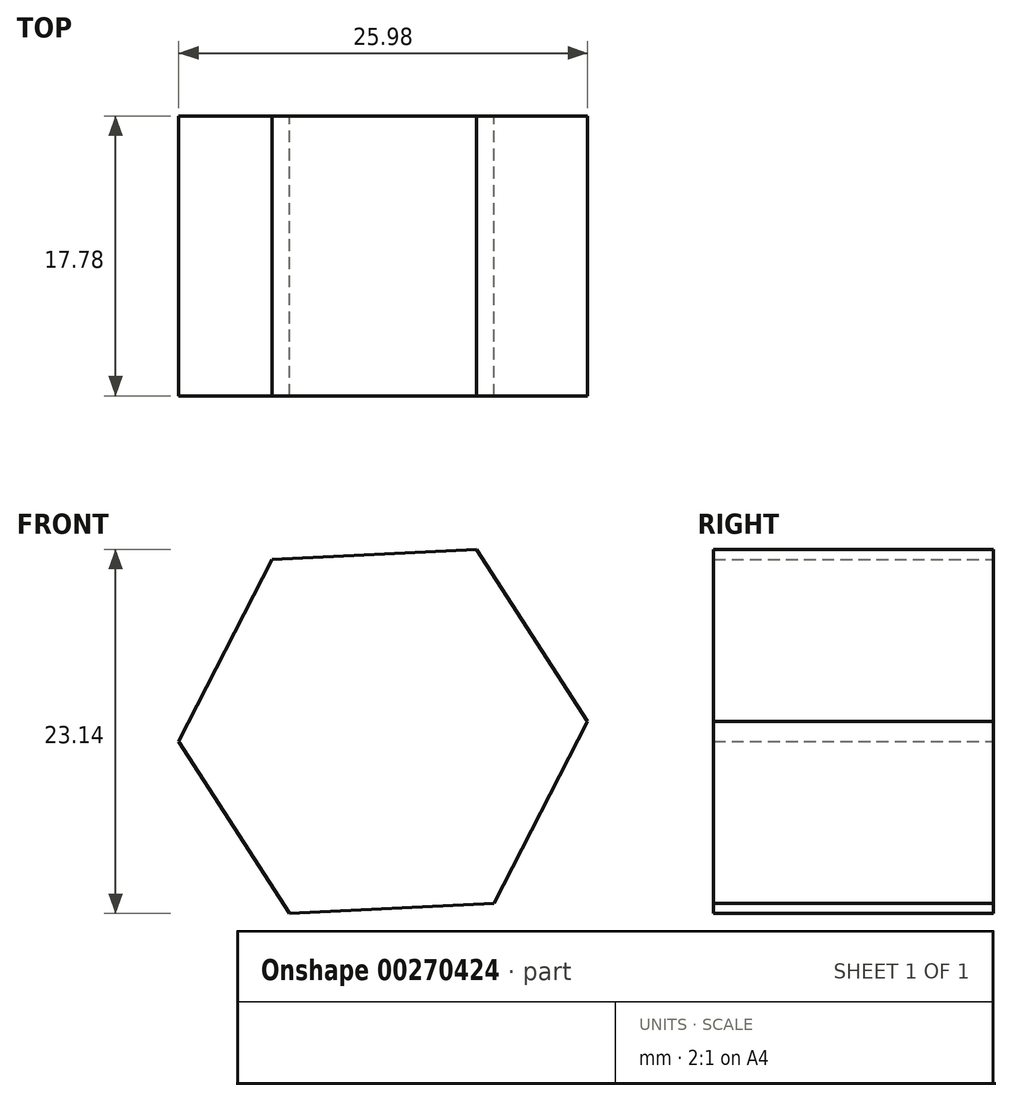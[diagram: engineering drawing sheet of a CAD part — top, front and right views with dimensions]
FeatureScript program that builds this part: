
annotation { "Feature Type Name" : "Feature", "Feature Type Description" : "" }
export const myFeature = defineFeature(function(context is Context, id is Id, definition is map)
    precondition{}
    {
        {
            var Q0;
            Q0=qCreatedBy(makeId("Front.planeOp"),FACE);
            var sketch = newSketch(context, id + "F0", { "sketchPlane" : qUnion([Q0])});
            skCircle(sketch, "E0.cCircle", {"center": v(0, 0) * mm, "radius": 11.26 * mm, "construction": true});
            skLineSegment(sketch, "E0.0", {"start": v(5.94, 11.57) * mm, "end": v(12.99, 0.64) * mm});
            skLineSegment(sketch, "E0.1", {"start": v(12.99, 0.64) * mm, "end": v(7.05, -10.93) * mm});
            skLineSegment(sketch, "E0.2", {"start": v(7.05, -10.93) * mm, "end": v(-5.94, -11.57) * mm});
            skLineSegment(sketch, "E0.3", {"start": v(-5.94, -11.57) * mm, "end": v(-12.99, -0.64) * mm});
            skLineSegment(sketch, "E0.4", {"start": v(-12.99, -0.64) * mm, "end": v(-7.05, 10.93) * mm});
            skLineSegment(sketch, "E0.5", {"start": v(-7.05, 10.93) * mm, "end": v(5.94, 11.57) * mm});
            skPoint(sketch, "E0.0.midPoint", {"position": v(9.46, 6.1) * mm});
            skSolve(sketch);
        }
        {
            var Q0;
            Q0=qCreatedBy(makeId("Top.planeOp"),FACE);
            var sketch = newSketch(context, id + "F1", { "sketchPlane" : qUnion([Q0])});
            skLineSegment(sketch, "E1", {"start": v(0, 0) * mm, "end": v(0, 17.78) * mm});
            skSolve(sketch);
        }
        {
            var Q0;
            Q0=makeQuery(id+"F0.imprint","IMPRINT",FACE,{"disambiguationData":[TD([[makeQuery(id+"F0.imprint","IMPRINT",EDGE,{"derivedFrom":sQuery(id+"F0.wireOp",EDGE,"E0.0")}),-1.0]])]});
            var Q1;
            Q1=sQuery(id+"F1.wireOp",EDGE,"E1");
            sweep(context, id + "F2", {"profiles" : qUnion([Q0]), "path" : qUnion([Q1])});
        }
    });
